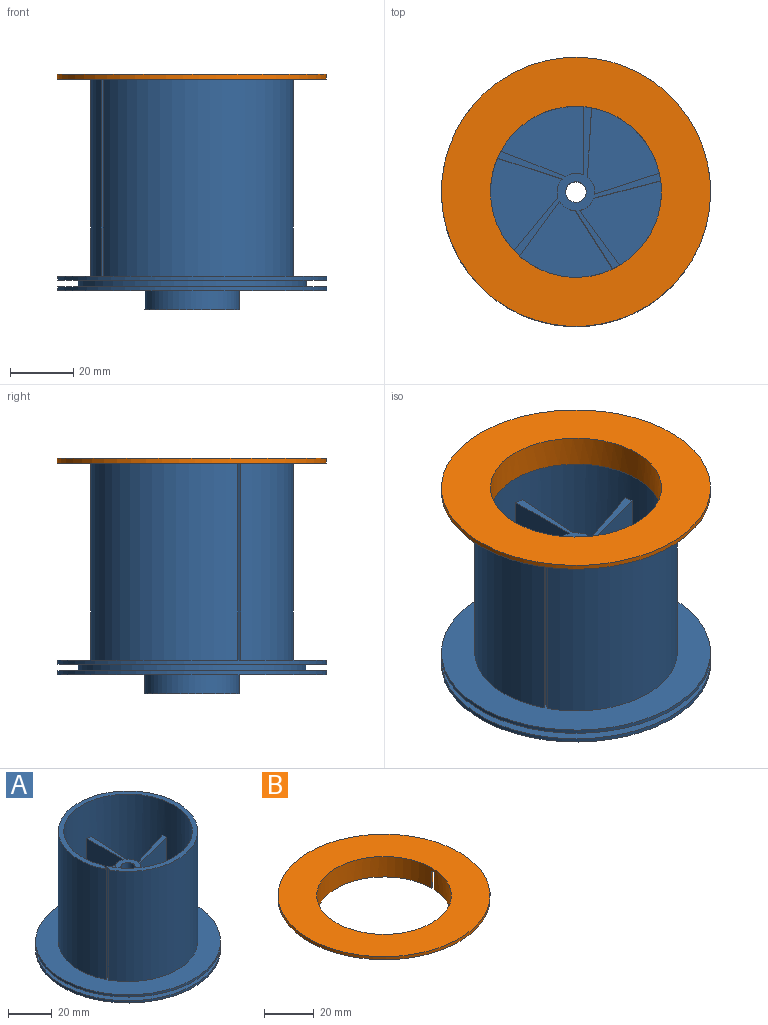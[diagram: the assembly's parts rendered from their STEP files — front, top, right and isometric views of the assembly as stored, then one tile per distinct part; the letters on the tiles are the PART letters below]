
ASSEMBLY  parts=2 mates=1
PART A: 35 faces, bbox 85x85x72.6 mm
  f0: plane 29.79x25.11mm, normal (0,0,1), area 480mm2, adj f8,f22,f23,f32
  f1: cylinder r=5.94mm len=42mm, axis (0,0,1), area 259mm2, adj f2,f9,f30,f31
  f2: plane 29.43x28.37mm, normal (0,0,1), area 480mm2, adj f1,f22,f30,f31
  f3: cylinder r=5.94mm len=42mm, axis (0,0,1), area 259mm2, adj f4,f9,f28,f29
  f4: plane 32.3x26.62mm, normal (0,0,1), area 480mm2, adj f3,f22,f28,f29
  f5: cylinder r=5.94mm len=42mm, axis (0,0,1), area 259mm2, adj f9,f19,f26,f27
  f6: cylinder r=5.94mm len=42mm, axis (0,0,1), area 259mm2, adj f7,f9,f24,f25
  f7: plane 28.59x24.6mm, normal (0,0,1), area 480mm2, adj f6,f22,f24,f25
  f8: cylinder r=5.94mm len=42mm, axis (0,0,1), area 259mm2, adj f0,f9,f23,f32
  f9: plane 56.38x55.88mm, normal (0,0,1), area 300.8mm2, adj f1,f3,f5,f6,f8,f10,f22,f23
  f10: cylinder r=3.25mm len=52.6mm, axis (0,0,1), area 1072.5mm2, adj f9,f11
  f11: plane 30x30mm, normal (0,0,-1), area 673.8mm2, adj f10,f12
  f12: cylinder r=15mm len=30mm, axis (0,0,1), area 565.5mm2, adj f11,f13
  f13: plane 85x85mm, normal (0,0,-1), area 4967.6mm2, adj f12,f14
  f14: cylinder r=42.5mm len=85mm, axis (0,0,1), area 333.8mm2, adj f13,f15
  f15: plane 85x85mm, normal (0,0,1), area 1603mm2, adj f14,f16
  f16: cylinder r=36mm len=72mm, axis (0,0,1), area 475mm2, adj f15,f17
  f17: plane 85x85mm, normal (0,0,-1), area 1603mm2, adj f16,f18
  f18: cylinder r=42.5mm len=85mm, axis (0,0,1), area 333.8mm2, adj f17,f19
  f19: plane 85x85mm, normal (0,0,1), area 2940.5mm2, adj f5,f18,f20,f22,f26,f27,f33,f34
  f20: cylinder r=32mm len=64mm, axis (0,0,1), area 12392.5mm2, adj f19,f21,f33,f34
  f21: plane 64x64mm, normal (0,0,1), area 480mm2, adj f20,f22,f33,f34
  f22: cylinder r=29.5mm len=62mm, axis (0,0,1), area 10876.9mm2, adj f0,f2,f4,f7,f9,f19,f21,f23
  f23: plane 42x24.35mm, normal (1,-0.06,0), area 1024.5mm2, adj f0,f8,f9,f22
  f24: plane 42x24.01mm, normal (-1,0,0), area 1008.2mm2, adj f6,f7,f9,f22
  f25: plane 42x22.72mm, normal (0.36,0.93,0), area 1024.5mm2, adj f6,f7,f9,f22
  f26: plane 42x22.83mm, normal (-0.31,-0.95,0), area 1008.2mm2, adj f5,f9,f19,f22
  f27: plane 42x18.86mm, normal (-0.77,0.63,0), area 1024.5mm2, adj f5,f9,f19,f22
  f28: plane 42x19.42mm, normal (0.81,-0.59,0), area 1008.2mm2, adj f3,f4,f9,f22
  f29: plane 42x20.54mm, normal (-0.84,-0.54,0), area 1024.5mm2, adj f3,f4,f9,f22
  f30: plane 42x19.42mm, normal (0.81,0.59,0), area 1008.2mm2, adj f1,f2,f9,f22
  f31: plane 42x23.6mm, normal (0.25,-0.97,0), area 1024.5mm2, adj f1,f2,f9,f22
  f32: plane 42x22.83mm, normal (-0.31,0.95,0), area 1008.2mm2, adj f0,f8,f9,f22
  f33: plane 62x2.64mm, normal (0.87,-0.5,0), area 189.1mm2, adj f19,f20,f21,f22
  f34: plane 62x2.57mm, normal (-0.87,0.5,0), area 184.1mm2, adj f19,f20,f21,f22
PART B: 9 faces, bbox 85x85x10 mm
  f0: cylinder r=27mm len=54mm, axis (0,0,1), area 1685.7mm2, adj f3,f5,f6,f7,f8
  f1: cylinder r=29mm len=58mm, axis (0,0,1), area 452.5mm2, adj f2,f5,f7,f8
  f2: cone r=29mm half-angle=6.7deg, axis (0,0,1), area 1080mm2, adj f1,f3,f7,f8
  f3: plane 56.6x56.6mm, normal (0,0,-1), area 224.2mm2, adj f0,f2,f7,f8
  f4: cylinder r=42.5mm len=85mm, axis (0,0,1), area 400.6mm2, adj f5,f6
  f5: plane 85x85mm, normal (0,0,-1), area 3034.9mm2, adj f0,f1,f4,f7,f8
  f6: plane 85x85mm, normal (0,0,1), area 3384.3mm2, adj f0,f4
  f7: plane 8.51x2.04mm, normal (-0.59,0.81,0), area 18.8mm2, adj f0,f1,f2,f3,f5
  f8: plane 8.51x1.98mm, normal (0.59,-0.81,0), area 18.2mm2, adj f0,f1,f2,f3,f5
PLACE A t=(0,0,30.5)mm fixed
PLACE B rot(axis=(0,0,-1),157.5deg) t=(0,0,63.5)mm
MATE cylindrical A.f1 <-> B.f4  axis (0,0,1) through (0,0,4.8)mm
